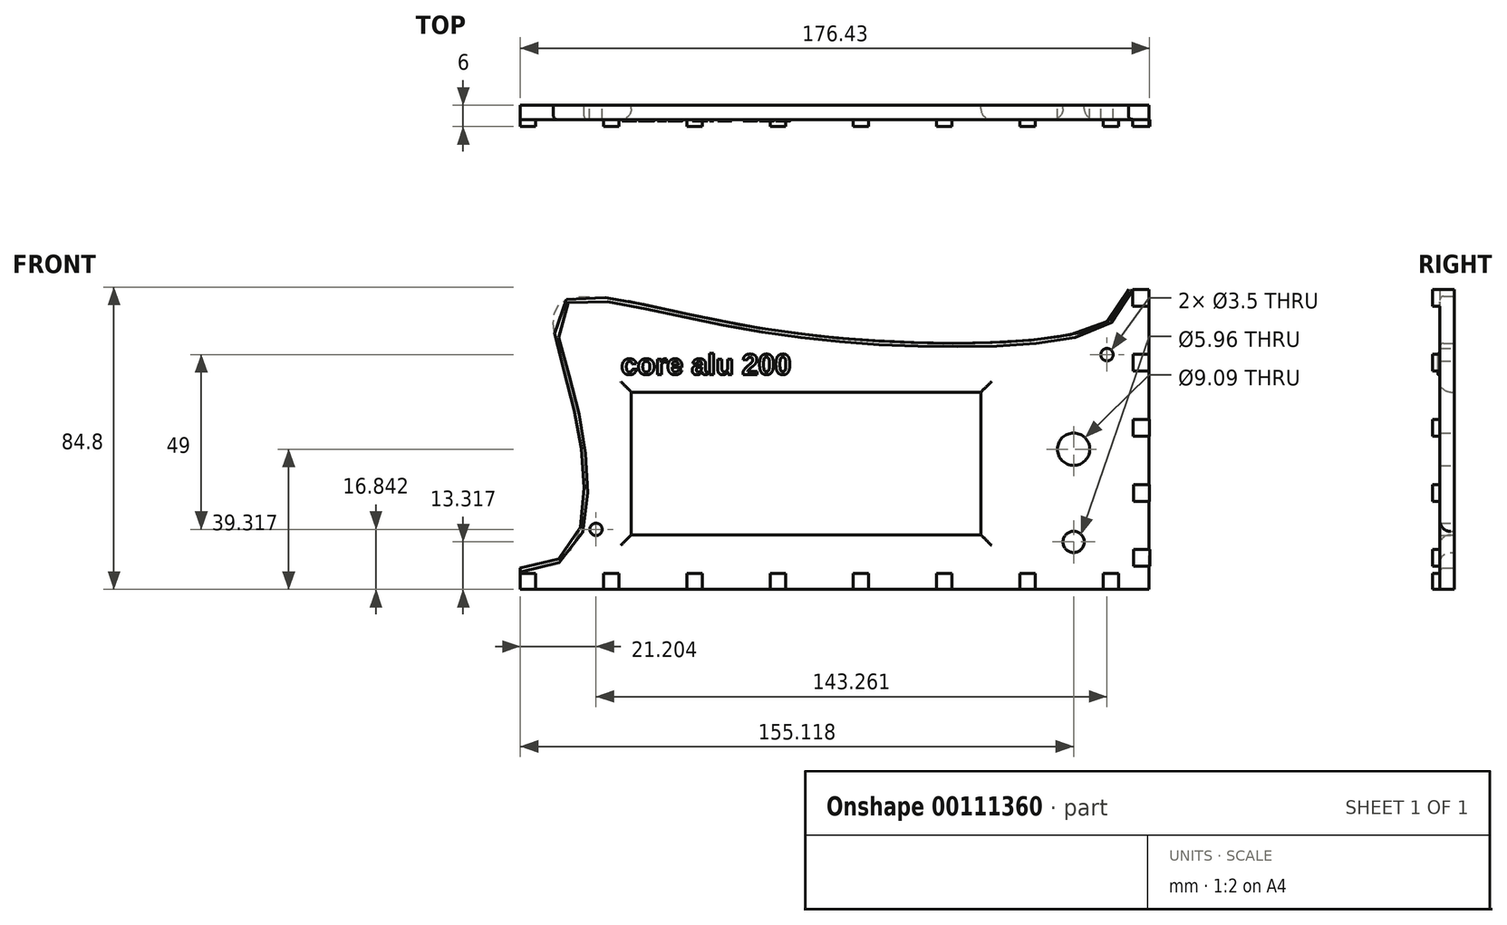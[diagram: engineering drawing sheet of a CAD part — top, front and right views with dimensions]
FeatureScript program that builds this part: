
annotation { "Feature Type Name" : "Feature", "Feature Type Description" : "" }
export const myFeature = defineFeature(function(context is Context, id is Id, definition is map)
    precondition{}
    {
        {
            var Q0;
            Q0=qCreatedBy(makeId("Front.planeOp"),FACE);
            var sketch = newSketch(context, id + "F0", { "sketchPlane" : qUnion([Q0])});
            skLineSegment(sketch, "E0.bottom", {"start": v(-77.31, 21.96) * mm, "end": v(72.69, 21.96) * mm, "construction": true});
            skLineSegment(sketch, "E0.top", {"start": v(-77.31, -41.04) * mm, "end": v(72.69, -41.04) * mm, "construction": true});
            skLineSegment(sketch, "E0.left", {"start": v(-77.31, 21.96) * mm, "end": v(-77.31, -41.04) * mm, "construction": true});
            skLineSegment(sketch, "E0.right", {"start": v(72.69, 21.96) * mm, "end": v(72.69, -41.04) * mm, "construction": true});
            skLineSegment(sketch, "E1", {"start": v(80.76, -46.36) * mm, "end": v(80.76, 37.8) * mm});
            skLineSegment(sketch, "E2", {"start": v(80.76, -46.36) * mm, "end": v(-95.43, -46.36) * mm});
            skLineSegment(sketch, "E3", {"start": v(-95.43, -46.36) * mm, "end": v(-95.43, -40.35) * mm});
            skLineSegment(sketch, "E4", {"start": v(80.76, 37.8) * mm, "end": v(75.04, 37.8) * mm});
            skFitSpline(sketch, "E5", {"points": [v(-95.43, -40.35) * mm, v(-82.26, -36.25) * mm, v(-78.93, -2.99) * mm, v(-85.2, 22.25) * mm, v(-85.4, 32.43) * mm, v(-78.74, 35.75) * mm, v(-51.35, 31.45) * mm, v(0, 23.62) * mm, v(62.52, 25.97) * mm, v(72.5, 32.43) * mm, v(75.04, 37.8) * mm, v(80.76, 37.8) * mm, v(80.76, -46.36) * mm, v(-95.43, -46.36) * mm, v(-95.43, -40.35) * mm]});
            skLineSegment(sketch, "E6.bottom", {"start": v(-64.31, 8.96) * mm, "end": v(33.69, 8.96) * mm});
            skLineSegment(sketch, "E6.top", {"start": v(-64.31, -31.04) * mm, "end": v(33.69, -31.04) * mm});
            skLineSegment(sketch, "E6.left", {"start": v(-64.31, 8.96) * mm, "end": v(-64.31, -31.04) * mm});
            skLineSegment(sketch, "E6.right", {"start": v(33.69, 8.96) * mm, "end": v(33.69, -31.04) * mm});
            skCircle(sketch, "E7", {"center": v(59.69, -7.04) * mm, "radius": 4.55 * mm});
            skCircle(sketch, "E8", {"center": v(59.69, -33.04) * mm, "radius": 2.98 * mm});
            skCircle(sketch, "E9", {"center": v(69.04, 19.48) * mm, "radius": 1.75 * mm});
            skCircle(sketch, "E10", {"center": v(69.63, -29.52) * mm, "radius": 1.75 * mm});
            skCircle(sketch, "E11", {"center": v(-74.23, -29.52) * mm, "radius": 1.75 * mm});
            skCircle(sketch, "E12", {"center": v(-74.96, 19.48) * mm, "radius": 1.75 * mm});
            skSolve(sketch);
        }
        {
            var Q0;
            Q0=makeQuery(id+"F0.imprint","IMPRINT",FACE,{"disambiguationData":[TD([[makeQuery(id+"F0.imprint","IMPRINT",EDGE,{"derivedFrom":sQuery(id+"F0.wireOp",EDGE,"E1")}),1.0]])]});
            var Q1;
            Q1=makeQuery(id+"F0.imprint","IMPRINT",FACE,{"disambiguationData":[TD([[makeQuery(id+"F0.imprint","IMPRINT",EDGE,{"derivedFrom":sQuery(id+"F0.wireOp",EDGE,"E10")}),1.0]])]});
            var Q2;
            Q2=makeQuery(id+"F0.imprint","IMPRINT",FACE,{"disambiguationData":[TD([[makeQuery(id+"F0.imprint","IMPRINT",EDGE,{"derivedFrom":sQuery(id+"F0.wireOp",EDGE,"E12")}),1.0]])]});
            extrude(context, id + "F1", {"entities" : qUnion([Q0, Q1, Q2]), "depth" : 4 * mm});
        }
        {
            var Q0;
            Q0=makeQuery(id+"F1.opExtrude","CAP_EDGE",EDGE,{"disambiguationData":[OSD([sQuery(id+"F0.wireOp",EDGE,"E5")])],"isStart":false});
            fillet(context, id + "F2", {"entities" : qUnion([Q0]), "radius" : 1 * mm, "tangentPropagation" : true, "allowEdgeOverflow" : false});
        }
        {
            var Q0;
            Q0=makeQuery(id+"F1.opExtrude","CAP_FACE",FACE,{"disambiguationData":[OSD([sQuery(id+"F0.wireOp",EDGE,"E1"),sQuery(id+"F0.wireOp",EDGE,"E2"),sQuery(id+"F0.wireOp",EDGE,"E3"),sQuery(id+"F0.wireOp",EDGE,"E4"),sQuery(id+"F0.wireOp",EDGE,"E5"),sQuery(id+"F0.wireOp",EDGE,"E6.bottom"),sQuery(id+"F0.wireOp",EDGE,"E6.top"),sQuery(id+"F0.wireOp",EDGE,"E6.left"),sQuery(id+"F0.wireOp",EDGE,"E6.right"),sQuery(id+"F0.wireOp",EDGE,"E7"),sQuery(id+"F0.wireOp",EDGE,"E8"),sQuery(id+"F0.wireOp",EDGE,"E9"),sQuery(id+"F0.wireOp",EDGE,"E11")])],"isStart":false});
            var sketch = newSketch(context, id + "F3", { "sketchPlane" : qUnion([Q0])});
            skLineSegment(sketch, "E13.bottom", {"start": v(-95.43, -46.36) * mm, "end": v(-91.12, -46.36) * mm});
            skLineSegment(sketch, "E13.top", {"start": v(-95.43, -41.86) * mm, "end": v(-91.12, -41.86) * mm});
            skLineSegment(sketch, "E13.left", {"start": v(-95.43, -46.36) * mm, "end": v(-95.43, -41.86) * mm});
            skLineSegment(sketch, "E13.right", {"start": v(-91.12, -46.36) * mm, "end": v(-91.12, -41.86) * mm});
            skLineSegment(sketch, "E14.1.0.0", {"start": v(-67.78, -46.36) * mm, "end": v(-67.78, -41.86) * mm});
            skLineSegment(sketch, "E14.1.0.1", {"start": v(-72.09, -46.36) * mm, "end": v(-72.09, -41.86) * mm});
            skLineSegment(sketch, "E14.1.0.2", {"start": v(-72.09, -41.86) * mm, "end": v(-67.78, -41.86) * mm});
            skLineSegment(sketch, "E14.1.0.3", {"start": v(-72.09, -46.36) * mm, "end": v(-67.78, -46.36) * mm});
            skLineSegment(sketch, "E14.2.0.0", {"start": v(-44.44, -46.36) * mm, "end": v(-44.44, -41.86) * mm});
            skLineSegment(sketch, "E14.2.0.1", {"start": v(-48.74, -46.36) * mm, "end": v(-48.74, -41.86) * mm});
            skLineSegment(sketch, "E14.2.0.2", {"start": v(-48.74, -41.86) * mm, "end": v(-44.44, -41.86) * mm});
            skLineSegment(sketch, "E14.2.0.3", {"start": v(-48.74, -46.36) * mm, "end": v(-44.44, -46.36) * mm});
            skLineSegment(sketch, "E14.3.0.0", {"start": v(-21.1, -46.36) * mm, "end": v(-21.1, -41.86) * mm});
            skLineSegment(sketch, "E14.3.0.1", {"start": v(-25.4, -46.36) * mm, "end": v(-25.4, -41.86) * mm});
            skLineSegment(sketch, "E14.3.0.2", {"start": v(-25.4, -41.86) * mm, "end": v(-21.1, -41.86) * mm});
            skLineSegment(sketch, "E14.3.0.3", {"start": v(-25.4, -46.36) * mm, "end": v(-21.1, -46.36) * mm});
            skLineSegment(sketch, "E14.4.0.0", {"start": v(2.24, -46.36) * mm, "end": v(2.24, -41.86) * mm});
            skLineSegment(sketch, "E14.4.0.1", {"start": v(-2.06, -46.36) * mm, "end": v(-2.06, -41.86) * mm});
            skLineSegment(sketch, "E14.4.0.2", {"start": v(-2.06, -41.86) * mm, "end": v(2.24, -41.86) * mm});
            skLineSegment(sketch, "E14.4.0.3", {"start": v(-2.06, -46.36) * mm, "end": v(2.24, -46.36) * mm});
            skLineSegment(sketch, "E14.5.0.0", {"start": v(25.59, -46.36) * mm, "end": v(25.59, -41.86) * mm});
            skLineSegment(sketch, "E14.5.0.1", {"start": v(21.28, -46.36) * mm, "end": v(21.28, -41.86) * mm});
            skLineSegment(sketch, "E14.5.0.2", {"start": v(21.28, -41.86) * mm, "end": v(25.59, -41.86) * mm});
            skLineSegment(sketch, "E14.5.0.3", {"start": v(21.28, -46.36) * mm, "end": v(25.59, -46.36) * mm});
            skLineSegment(sketch, "E14.6.0.0", {"start": v(48.93, -46.36) * mm, "end": v(48.93, -41.86) * mm});
            skLineSegment(sketch, "E14.6.0.1", {"start": v(44.62, -46.36) * mm, "end": v(44.62, -41.86) * mm});
            skLineSegment(sketch, "E14.6.0.2", {"start": v(44.62, -41.86) * mm, "end": v(48.93, -41.86) * mm});
            skLineSegment(sketch, "E14.6.0.3", {"start": v(44.62, -46.36) * mm, "end": v(48.93, -46.36) * mm});
            skLineSegment(sketch, "E14.7.0.0", {"start": v(72.27, -46.36) * mm, "end": v(72.27, -41.86) * mm});
            skLineSegment(sketch, "E14.7.0.1", {"start": v(67.97, -46.36) * mm, "end": v(67.97, -41.86) * mm});
            skLineSegment(sketch, "E14.7.0.2", {"start": v(67.97, -41.86) * mm, "end": v(72.27, -41.86) * mm});
            skLineSegment(sketch, "E14.7.0.3", {"start": v(67.97, -46.36) * mm, "end": v(72.27, -46.36) * mm});
            skLineSegment(sketch, "E14.direction1", {"start": v(-95.43, -46.36) * mm, "end": v(-72.09, -46.36) * mm, "construction": true});
            skLineSegment(sketch, "E15.bottom", {"start": v(80.76, 37.8) * mm, "end": v(76.26, 37.8) * mm});
            skLineSegment(sketch, "E15.top", {"start": v(80.76, 33.08) * mm, "end": v(76.26, 33.08) * mm});
            skLineSegment(sketch, "E15.left", {"start": v(80.76, 37.8) * mm, "end": v(80.76, 33.08) * mm});
            skLineSegment(sketch, "E15.right", {"start": v(76.26, 37.8) * mm, "end": v(76.26, 33.08) * mm});
            skLineSegment(sketch, "E16.1.0.0", {"start": v(80.82, 19.56) * mm, "end": v(80.82, 14.84) * mm});
            skLineSegment(sketch, "E16.1.0.1", {"start": v(80.82, 14.84) * mm, "end": v(76.32, 14.84) * mm});
            skLineSegment(sketch, "E16.1.0.2", {"start": v(80.82, 19.56) * mm, "end": v(76.32, 19.56) * mm});
            skLineSegment(sketch, "E16.1.0.3", {"start": v(76.32, 19.56) * mm, "end": v(76.32, 14.84) * mm});
            skLineSegment(sketch, "E16.2.0.0", {"start": v(80.88, 1.32) * mm, "end": v(80.88, -3.4) * mm});
            skLineSegment(sketch, "E16.2.0.1", {"start": v(80.88, -3.4) * mm, "end": v(76.38, -3.4) * mm});
            skLineSegment(sketch, "E16.2.0.2", {"start": v(80.88, 1.32) * mm, "end": v(76.38, 1.32) * mm});
            skLineSegment(sketch, "E16.2.0.3", {"start": v(76.38, 1.32) * mm, "end": v(76.38, -3.4) * mm});
            skLineSegment(sketch, "E16.3.0.0", {"start": v(80.94, -16.92) * mm, "end": v(80.94, -21.64) * mm});
            skLineSegment(sketch, "E16.3.0.1", {"start": v(80.94, -21.64) * mm, "end": v(76.44, -21.64) * mm});
            skLineSegment(sketch, "E16.3.0.2", {"start": v(80.94, -16.92) * mm, "end": v(76.44, -16.92) * mm});
            skLineSegment(sketch, "E16.3.0.3", {"start": v(76.44, -16.92) * mm, "end": v(76.44, -21.64) * mm});
            skLineSegment(sketch, "E16.4.0.0", {"start": v(81, -35.16) * mm, "end": v(81, -39.88) * mm});
            skLineSegment(sketch, "E16.4.0.1", {"start": v(81, -39.88) * mm, "end": v(76.5, -39.88) * mm});
            skLineSegment(sketch, "E16.4.0.2", {"start": v(81, -35.16) * mm, "end": v(76.5, -35.16) * mm});
            skLineSegment(sketch, "E16.4.0.3", {"start": v(76.5, -35.16) * mm, "end": v(76.5, -39.88) * mm});
            skLineSegment(sketch, "E16.direction1", {"start": v(76.26, 33.08) * mm, "end": v(76.32, 14.84) * mm, "construction": true});
            skSolve(sketch);
        }
        {
            var Q0;
            Q0 = qSketchRegion(id + "F3", true);
            extrude(context, id + "F4", {"entities" : qUnion([Q0]), "operationType" : NewBodyOperationType.ADD, "depth" : 2 * mm});
        }
        {
            var Q0;
            Q0=makeQuery(id+"F1.opExtrude","CAP_EDGE",EDGE,{"disambiguationData":[OSD([sQuery(id+"F0.wireOp",EDGE,"E6.bottom")])],"isStart":false});
            var Q1;
            Q1=makeQuery(id+"F1.opExtrude","CAP_EDGE",EDGE,{"disambiguationData":[OSD([sQuery(id+"F0.wireOp",EDGE,"E6.right")])],"isStart":false});
            var Q2;
            Q2=makeQuery(id+"F1.opExtrude","CAP_EDGE",EDGE,{"disambiguationData":[OSD([sQuery(id+"F0.wireOp",EDGE,"E6.top")])],"isStart":false});
            var Q3;
            Q3=makeQuery(id+"F1.opExtrude","CAP_EDGE",EDGE,{"disambiguationData":[OSD([sQuery(id+"F0.wireOp",EDGE,"E6.left")])],"isStart":false});
            fillet(context, id + "F5", {"entities" : qUnion([Q0, Q1, Q2, Q3]), "radius" : 3 * mm, "tangentPropagation" : true, "allowEdgeOverflow" : false});
        }
        {
            var Q0;
            Q0=makeQuery(id+"F1.opExtrude","CAP_EDGE",EDGE,{"disambiguationData":[OSD([sQuery(id+"F0.wireOp",EDGE,"E8")])],"isStart":false});
            fillet(context, id + "F6", {"entities" : qUnion([Q0]), "radius" : 3 * mm, "tangentPropagation" : true, "allowEdgeOverflow" : false});
        }
        {
            var Q0;
            Q0=makeQuery(id+"F1.opExtrude","CAP_FACE",FACE,{"disambiguationData":[OSD([sQuery(id+"F0.wireOp",EDGE,"E1"),sQuery(id+"F0.wireOp",EDGE,"E2"),sQuery(id+"F0.wireOp",EDGE,"E3"),sQuery(id+"F0.wireOp",EDGE,"E4"),sQuery(id+"F0.wireOp",EDGE,"E5"),sQuery(id+"F0.wireOp",EDGE,"E6.bottom"),sQuery(id+"F0.wireOp",EDGE,"E6.top"),sQuery(id+"F0.wireOp",EDGE,"E6.left"),sQuery(id+"F0.wireOp",EDGE,"E6.right"),sQuery(id+"F0.wireOp",EDGE,"E7"),sQuery(id+"F0.wireOp",EDGE,"E8"),sQuery(id+"F0.wireOp",EDGE,"E9"),sQuery(id+"F0.wireOp",EDGE,"E11")])],"isStart":false});
            var sketch = newSketch(context, id + "F7", { "sketchPlane" : qUnion([Q0])});
            skText(sketch, "E17", { "text": "core alu 200", "fontName": "Arimo-Bold.ttf"});
            const initialGuessF7  = {"E17": [-0.06722, 0.0139, 1, 0, 0.00594]};
            skSetInitialGuess(sketch, initialGuessF7);
            skSolve(sketch);
        }
        {
            var Q0;
            Q0 = qSketchRegion(id + "F7", true);
            extrude(context, id + "F8", {"entities" : qUnion([Q0]), "operationType" : NewBodyOperationType.ADD, "depth" : 0.5 * mm});
        }
    });
